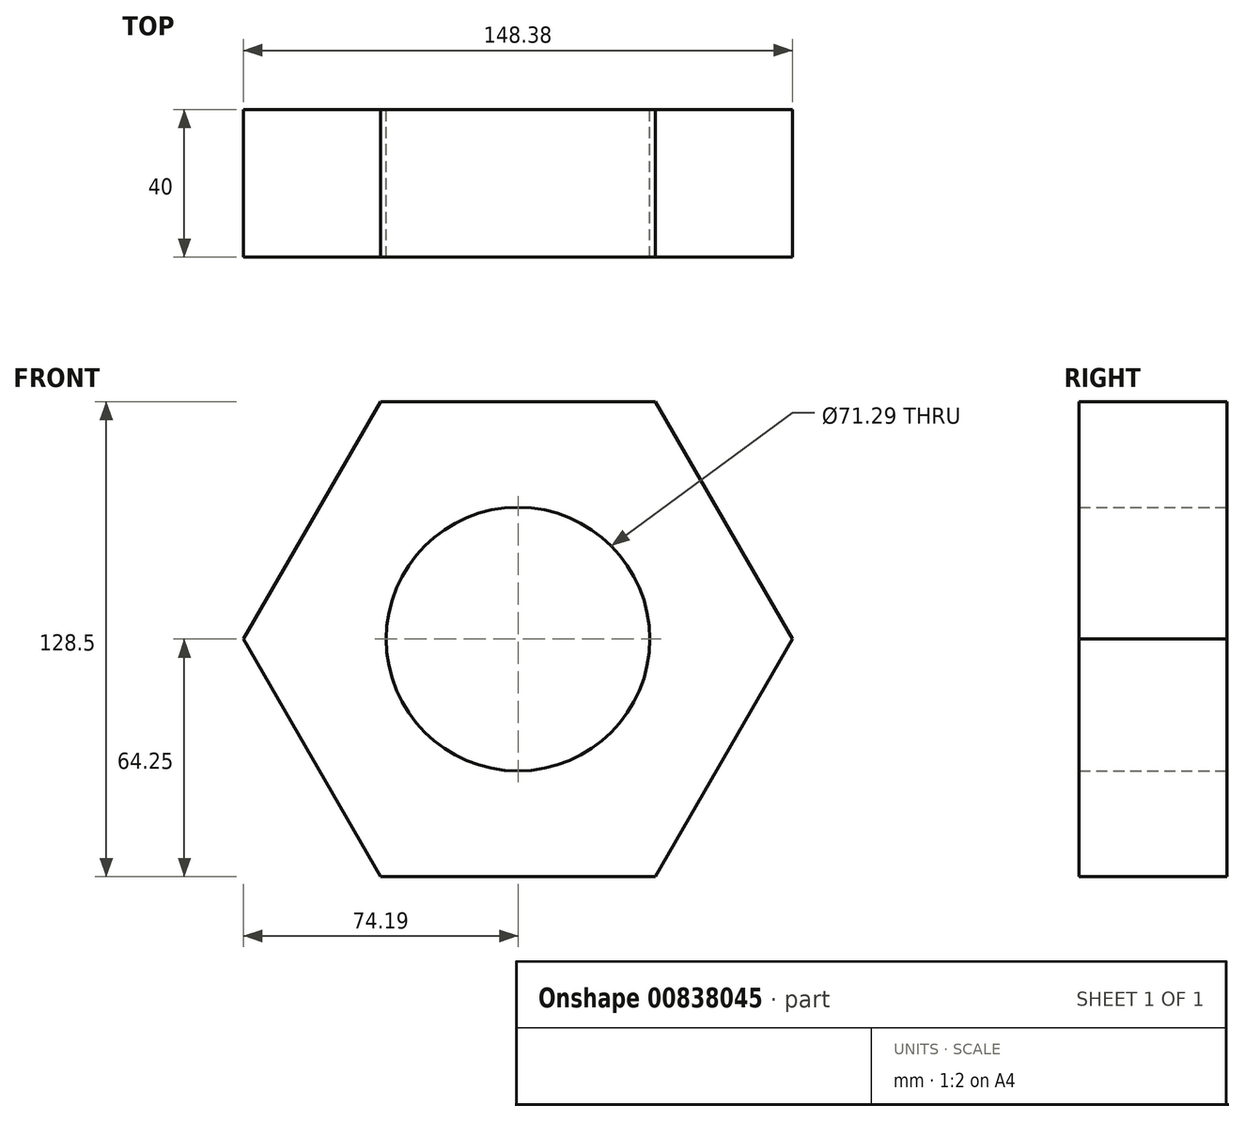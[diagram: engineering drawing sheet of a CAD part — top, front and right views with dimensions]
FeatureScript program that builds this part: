
annotation { "Feature Type Name" : "Feature", "Feature Type Description" : "" }
export const myFeature = defineFeature(function(context is Context, id is Id, definition is map)
    precondition{}
    {
        {
            var Q0;
            Q0=qCreatedBy(makeId("Front.planeOp"),FACE);
            var sketch = newSketch(context, id + "F0", { "sketchPlane" : qUnion([Q0])});
            skCircle(sketch, "E0.cCircle", {"center": v(0, 0) * mm, "radius": 74.19 * mm, "construction": true});
            skLineSegment(sketch, "E0.0", {"start": v(74.19, 0) * mm, "end": v(37.1, -64.25) * mm});
            skLineSegment(sketch, "E0.1", {"start": v(37.1, -64.25) * mm, "end": v(-37.1, -64.25) * mm});
            skLineSegment(sketch, "E0.2", {"start": v(-37.1, -64.25) * mm, "end": v(-74.19, 0) * mm});
            skLineSegment(sketch, "E0.3", {"start": v(-74.19, 0) * mm, "end": v(-37.1, 64.25) * mm});
            skLineSegment(sketch, "E0.4", {"start": v(-37.1, 64.25) * mm, "end": v(37.1, 64.25) * mm});
            skLineSegment(sketch, "E0.5", {"start": v(37.1, 64.25) * mm, "end": v(74.19, 0) * mm});
            skCircle(sketch, "E1", {"center": v(0, 0) * mm, "radius": 35.64 * mm});
            skSolve(sketch);
        }
        {
            var Q0;
            Q0 = qSketchRegion(id + "F0", true);
            extrude(context, id + "F1", {"entities" : qUnion([Q0]), "depth" : 40 * mm, "offsetDistance" : 25 * mm});
        }
    });
